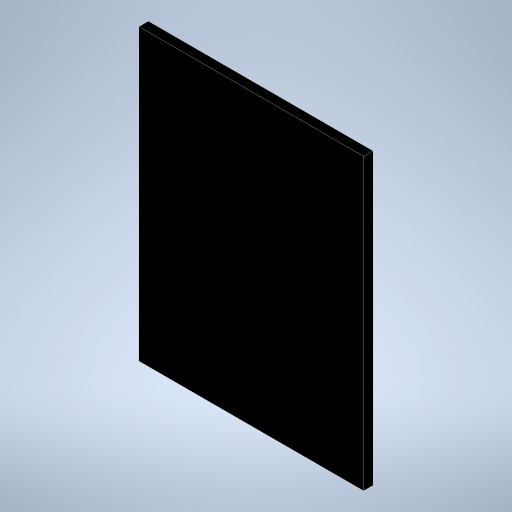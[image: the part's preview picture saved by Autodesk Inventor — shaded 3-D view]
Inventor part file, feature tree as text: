
AUTODESK INVENTOR PART (.ipt)
format: ipt  version: 2023.2 (Build 272271030, 271C)  size: 203,776 bytes
history: native  units: in
note: dims shown in document units (in); Inventor stores cm internally (conversion verified against a paired STEP export)
features: other x1, extrude x1, sketch x1
ambient origin geometry x8: Origin, YZ Plane, XZ Plane, XY Plane, X Axis, Y Axis, Z Axis, Center Point
bodies: Solid1 (feature_tree)
feature tree (3):
  other  "BoardFrontPlane"
  extrude  "BoardOutline"  [1 undecoded]
  sketch  "Sketch1"  dims[d0=0.0628in d1=0.0in]
note: 1 required parameter value undecoded (feature->parameter linkage not recoverable at this tier; creation-order binding heuristic only, values carry confidence <= 0.55)
